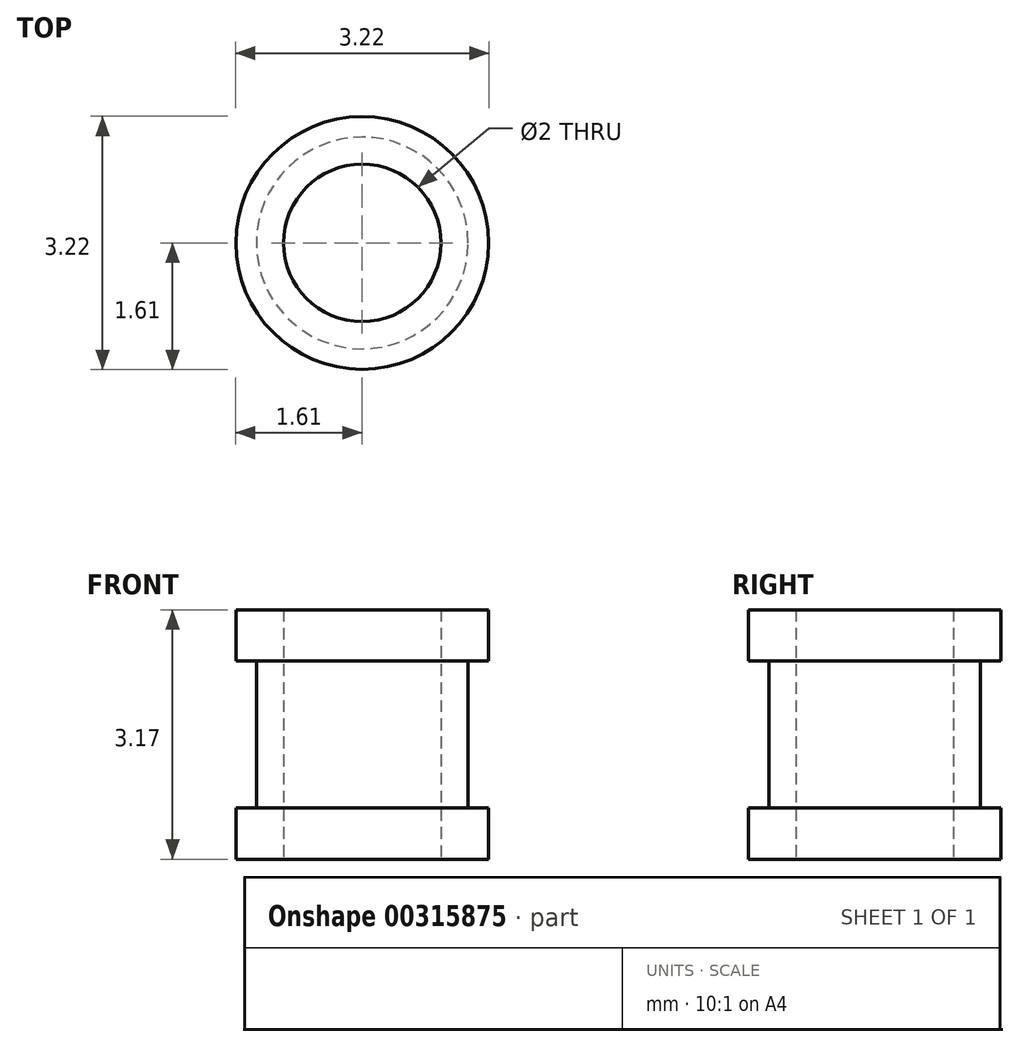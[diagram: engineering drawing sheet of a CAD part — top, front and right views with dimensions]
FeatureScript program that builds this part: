
annotation { "Feature Type Name" : "Feature", "Feature Type Description" : "" }
export const myFeature = defineFeature(function(context is Context, id is Id, definition is map)
    precondition{}
    {
        {
            var Q0;
            Q0=qCreatedBy(makeId("Top.planeOp"),FACE);
            var sketch = newSketch(context, id + "F0", { "sketchPlane" : qUnion([Q0])});
            skCircle(sketch, "E0", {"center": v(0, 0) * mm, "radius": 1.6 * mm});
            skCircle(sketch, "E1", {"center": v(0, 0) * mm, "radius": 1 * mm});
            skSolve(sketch);
        }
        {
            var Q0;
            Q0=makeQuery(id+"F0.imprint","IMPRINT",FACE,{"disambiguationData":[TD([[makeQuery(id+"F0.imprint","IMPRINT",EDGE,{"derivedFrom":sQuery(id+"F0.wireOp",EDGE,"E0")}),1.0]])]});
            extrude(context, id + "F1", {"entities" : qUnion([Q0]), "depth" : 3.17 * mm});
        }
        {
            var Q0;
            Q0=makeQuery(id+"F1.opExtrude","CAP_FACE",FACE,{"disambiguationData":[OSD([sQuery(id+"F0.wireOp",EDGE,"E0"),sQuery(id+"F0.wireOp",EDGE,"E1")])],"isStart":false});
            var sketch = newSketch(context, id + "F2", { "sketchPlane" : qUnion([Q0])});
            skCircle(sketch, "E2", {"center": v(0, 0) * mm, "radius": 1.34 * mm});
            skCircle(sketch, "E3", {"center": v(0, 0) * mm, "radius": 1.93 * mm});
            skSolve(sketch);
        }
        {
            var Q0;
            Q0=makeQuery(id+"F2.imprint","IMPRINT",FACE,{"disambiguationData":[TD([[makeQuery(id+"F2.imprint","IMPRINT",EDGE,{"derivedFrom":sQuery(id+"F2.wireOp",EDGE,"E2")}),-1.0]])]});
            extrude(context, id + "F3", {"entities" : qUnion([Q0]), "operationType" : NewBodyOperationType.REMOVE, "oppositeDirection" : true, "depth" : 2.52 * mm});
        }
        {
            var Q0;
            Q0=makeQuery(id+"F1.opExtrude","CAP_FACE",FACE,{"disambiguationData":[OSD([sQuery(id+"F0.wireOp",EDGE,"E0"),sQuery(id+"F0.wireOp",EDGE,"E1")])],"isStart":false});
            var sketch = newSketch(context, id + "F4", { "sketchPlane" : qUnion([Q0])});
            skCircle(sketch, "E4", {"center": v(0, 0) * mm, "radius": 1.34 * mm});
            skCircle(sketch, "E5", {"center": v(0, 0) * mm, "radius": 1.6 * mm});
            skSolve(sketch);
        }
        {
            var Q0;
            Q0=makeQuery(id+"F4.imprint","IMPRINT",FACE,{"disambiguationData":[TD([[makeQuery(id+"F4.imprint","IMPRINT",EDGE,{"derivedFrom":sQuery(id+"F4.wireOp",EDGE,"E4")}),-1.0]])]});
            extrude(context, id + "F5", {"entities" : qUnion([Q0]), "oppositeDirection" : true, "depth" : .65 * mm});
        }
        {
            var Q0;
            Q0=makeQuery(id+"F5.opExtrude","SWEPT_BODY",BODY,{"disambiguationData":[OSD([sQuery(id+"F4.wireOp",EDGE,"E4"),sQuery(id+"F4.wireOp",EDGE,"E5")])]});
            deleteBodies(context, id + "F6", {"entities" : qUnion([Q0])});
        }
        {
            var Q0;
            Q0 = qSketchRegion(id + "F4", true);
            extrude(context, id + "F7", {"entities" : qUnion([Q0]), "operationType" : NewBodyOperationType.ADD, "oppositeDirection" : true, "depth" : .65 * mm});
        }
    });
